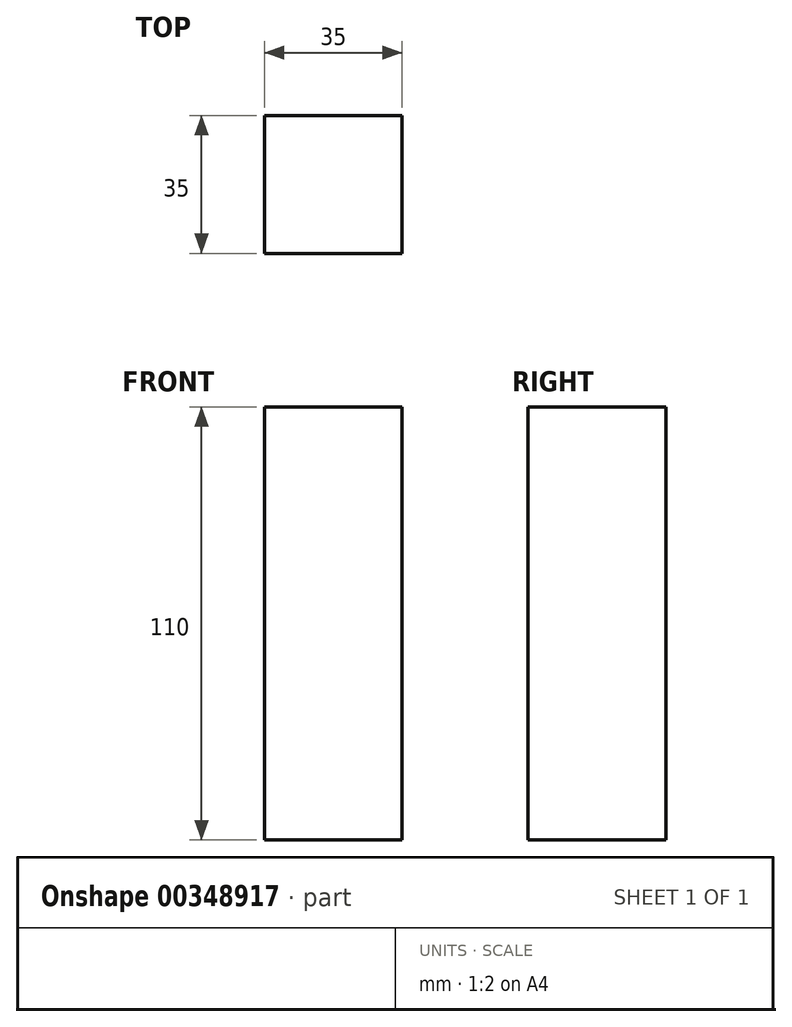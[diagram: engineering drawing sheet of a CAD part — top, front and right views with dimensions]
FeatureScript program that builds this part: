
annotation { "Feature Type Name" : "Feature", "Feature Type Description" : "" }
export const myFeature = defineFeature(function(context is Context, id is Id, definition is map)
    precondition{}
    {
        {
            var Q0;
            Q0=qCreatedBy(makeId("Top.planeOp"),FACE);
            var sketch = newSketch(context, id + "F0", { "sketchPlane" : qUnion([Q0])});
            skLineSegment(sketch, "E0.bottom", {"start": v(-2.9, 0.55) * mm, "end": v(-37.9, 0.55) * mm});
            skLineSegment(sketch, "E0.top", {"start": v(-2.9, 35.55) * mm, "end": v(-37.9, 35.55) * mm});
            skLineSegment(sketch, "E0.left", {"start": v(-2.9, 0.55) * mm, "end": v(-2.9, 35.55) * mm});
            skLineSegment(sketch, "E0.right", {"start": v(-37.9, 0.55) * mm, "end": v(-37.9, 35.55) * mm});
            skSolve(sketch);
        }
        {
            var Q0;
            Q0=makeQuery(id+"F0.imprint","IMPRINT",FACE,{"disambiguationData":[TD([[makeQuery(id+"F0.imprint","IMPRINT",EDGE,{"derivedFrom":sQuery(id+"F0.wireOp",EDGE,"E0.bottom")}),-1.0]])]});
            extrude(context, id + "F1", {"entities" : qUnion([Q0]), "depth" : (110) * mm});
        }
    });
